# Revit family: KEUCO_59556011202
name_source: partatom
category: Allgemeines Modell
revit_build: Autodesk Revit 2016 (Build: 20150220_1215(x64)
units: mm (PartAtom-declared; Revit-internal decimal feet)

## family parameters
Arbeitsebenenbasiert = Ja
Beim Laden mit Abzugskörper schneiden = Nein
Bemaßung runder Anschluss = Durchmesser verwenden
Gemeinsam genutzt = Nein
Immer vertikal = Nein
Kann Basisbauteil für Bewehrung sein = Nein
Raumberechnungspunkt = Nein
Teiletyp = Normal

## types (1)
- 59556011202
    Artikelnummer = 59556011202
    Ausschreibungstext = KEUCO IXMO 2-Wege Umstellventil mit Schlauchanschluss 
und Brausehalter UP DN15, 59556011202
2–Wege Umstellventil aus hochglanzverchromten Messing 
mit IXMO Griff Comfort und Schlauchanschluss 
sowie integriertem Brausehalter,
frei positionierbar, eigensicher gegen Rückfließen,
integrierter Einbautiefenausgleich von 80-110 mm,
mit Justier-Möglichkeit bei Feinmontage 
für Bedienteil und Rosette,
mit eckiger Rosette, Schlauchanschluss G 1/2 Zoll,
für Schläuche mit konischer Mutter,
z.B. KEUCO Brauseschlauch 54995...,
Rosette 90 x 90 mm, Stärke 10 mm,
Gesamtausladung 80 mm,
Fertigset bestehend aus: 
Griff, Gehäuse, Rosette (eckig) und Umstellventil,
passend für UP Funktionseinheit Art.–Nr. 59556000170
    Beschreibung = für Schläuche mit konischer Mutter
Fertigset bestehend aus:
Griff, Gehäuse, Rosette (eckig) und Umstellventil,
eigensicher gegen Rückfließen, nach DIN EN 1717,
passend für UP Funktionseinheit Art.-Nr. 59556 000170
    Breite = 45 mm  [stored 0.147638 ft]
    Gewicht = 0
    Hersteller = KEUCO
    Material = Stahl, verchromt
    Serie = Plan
    URL = https://www.keuco.com
    Verwendung = DU / WA
    Vorgabe-Ansicht = 1219 mm

note: [stored X ft] marks values corroborated as IEEE doubles in the binary element streams (Revit-internal decimal feet)

## geometry (parser evidence)
native form markers: Sweep x3
no freeform markers — native parametric forms only
